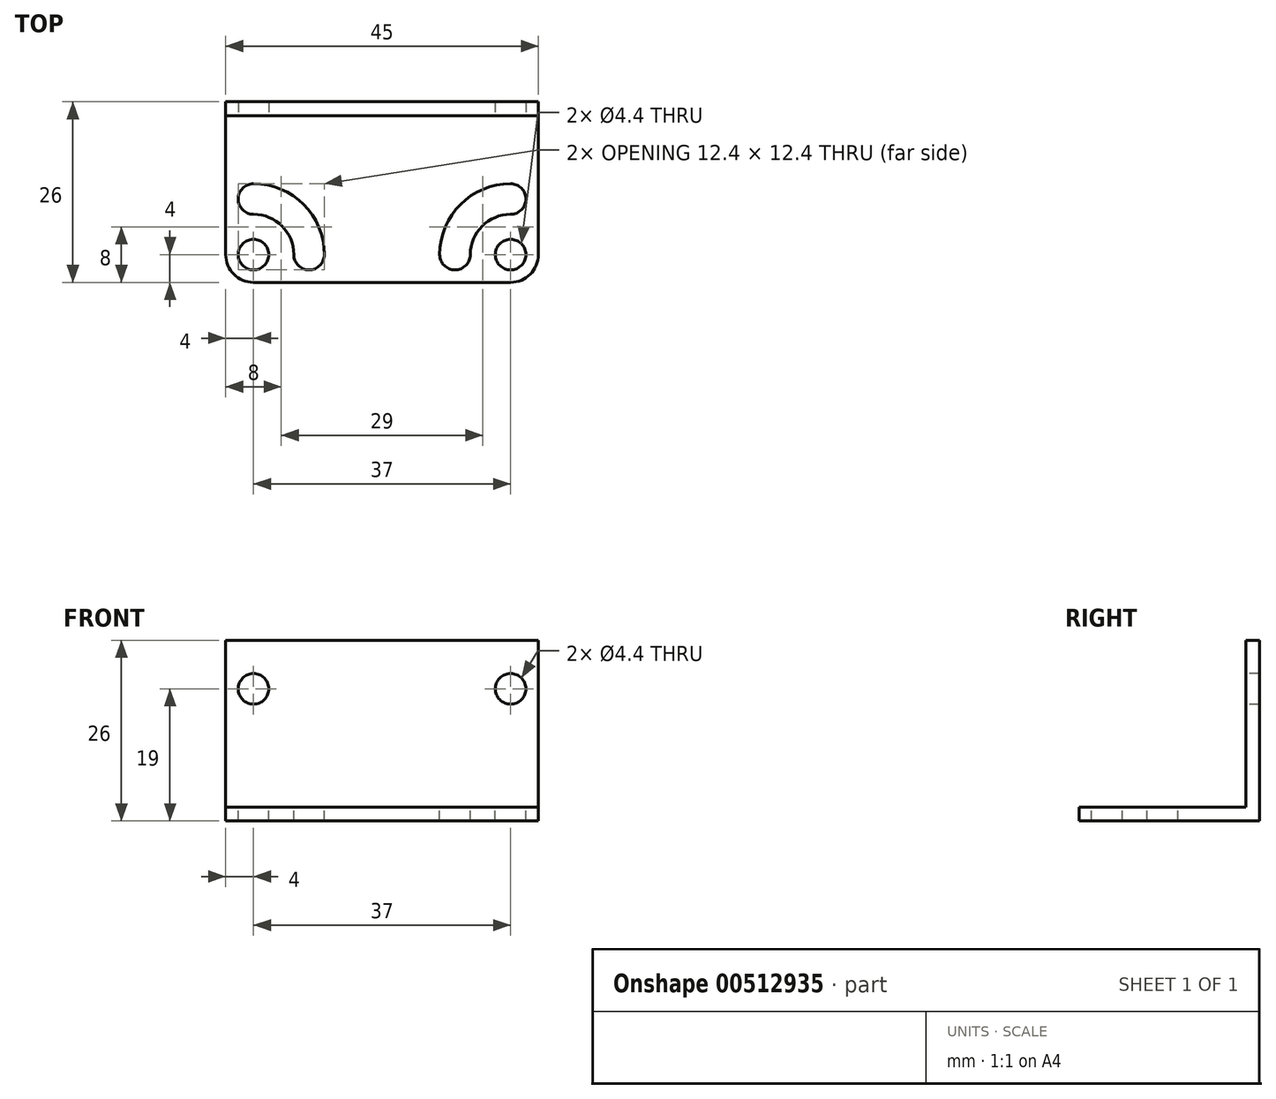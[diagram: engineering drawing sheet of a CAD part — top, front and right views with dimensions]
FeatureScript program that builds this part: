
annotation { "Feature Type Name" : "Feature", "Feature Type Description" : "" }
export const myFeature = defineFeature(function(context is Context, id is Id, definition is map)
    precondition{}
    {
        {
            var Q0;
            Q0=qCreatedBy(makeId("Top.planeOp"),FACE);
            var sketch = newSketch(context, id + "F0", { "sketchPlane" : qUnion([Q0])});
            skLineSegment(sketch, "E0.bottom", {"start": v(-22.5, 13) * mm, "end": v(22.5, 13) * mm});
            skLineSegment(sketch, "E0.top", {"start": v(-22.5, -13) * mm, "end": v(22.5, -13) * mm});
            skLineSegment(sketch, "E0.left", {"start": v(-22.5, 13) * mm, "end": v(-22.5, -13) * mm});
            skLineSegment(sketch, "E0.right", {"start": v(22.5, 13) * mm, "end": v(22.5, -13) * mm});
            skSolve(sketch);
        }
        {
            var Q0;
            Q0 = qSketchRegion(id + "F0", true);
            extrude(context, id + "F1", {"entities" : qUnion([Q0]), "depth" : 26 * mm});
        }
        {
            var Q0;
            Q0=makeQuery(id+"F1.opExtrude","SWEPT_FACE",FACE,{"disambiguationData":[OSD([sQuery(id+"F0.wireOp",EDGE,"E0.right")])]});
            var sketch = newSketch(context, id + "F2", { "sketchPlane" : qUnion([Q0])});
            skLineSegment(sketch, "E1.bottom", {"start": v(-13, 26) * mm, "end": v(11, 26) * mm});
            skLineSegment(sketch, "E1.top", {"start": v(-13, 2) * mm, "end": v(11, 2) * mm});
            skLineSegment(sketch, "E1.left", {"start": v(-13, 26) * mm, "end": v(-13, 2) * mm});
            skLineSegment(sketch, "E1.right", {"start": v(11, 26) * mm, "end": v(11, 2) * mm});
            skSolve(sketch);
        }
        {
            var Q0;
            Q0 = qSketchRegion(id + "F2", true);
            extrude(context, id + "F3", {"entities" : qUnion([Q0]), "operationType" : NewBodyOperationType.REMOVE, "endBound" : BoundingType.THROUGH_ALL, "oppositeDirection" : true, "depth" : 25 * mm});
        }
        {
            var Q0;
            Q0=makeQuery(id+"F3.boolean.opBoolean","COPY",FACE,{"derivedFrom":makeQuery(id+"F3.opExtrude","SWEPT_FACE",FACE,{"disambiguationData":[OSD([sQuery(id+"F2.wireOp",EDGE,"E1.top")])]})});
            var sketch = newSketch(context, id + "F4", { "sketchPlane" : qUnion([Q0])});
            skPoint(sketch, "E2", {"position": v(-18.5, -9) * mm});
            skPoint(sketch, "E3", {"position": v(-12.98, -3.21) * mm});
            skPoint(sketch, "E4.MirrorP", {"position": v(18.5, -9) * mm});
            skSolve(sketch);
        }
        {
            var Q0;
            Q0=sQuery(id+"F4.wireOp",VERTEX,"E2");
            var Q1;
            Q1=sQuery(id+"F4.wireOp",VERTEX,"E4.MirrorP");
            var Q2;
            Q2=makeQuery(id+"F1.opExtrude","SWEPT_BODY",BODY,{"disambiguationData":[OSD([sQuery(id+"F0.wireOp",EDGE,"E0.bottom"),sQuery(id+"F0.wireOp",EDGE,"E0.top"),sQuery(id+"F0.wireOp",EDGE,"E0.left"),sQuery(id+"F0.wireOp",EDGE,"E0.right")])]});
            hole(context, id + "F5", {"style" : HoleStyle.SIMPLE, "endStyle" : HoleEndStyle.THROUGH, "standardTappedOrClearance" : lookupTablePath({ "standard" : "ISO", "fit" : "Normal", "size" : "M4", "type" : "Clearance" }), "standardBlindInLast" : lookupTablePath({ "fit" : "Standard", "standard" : "ISO", "size" : "M4", "type" : "Clearance" }), "holeDiameter" : 4.4 * mm, "isTappedThrough" : true, "tappedDepth" : 12 * mm, "tapClearance" : 3, "locations" : qUnion([Q0, Q1]), "scope" : qUnion([Q2])});
        }
        {
            var Q0;
            Q0=makeQuery(id+"F3.boolean.opBoolean","COPY",FACE,{"derivedFrom":makeQuery(id+"F3.opExtrude","SWEPT_FACE",FACE,{"disambiguationData":[OSD([sQuery(id+"F2.wireOp",EDGE,"E1.right")])]})});
            var sketch = newSketch(context, id + "F6", { "sketchPlane" : qUnion([Q0])});
            skPoint(sketch, "E5", {"position": v(-18.5, 19) * mm});
            skPoint(sketch, "E6", {"position": v(18.5, 19) * mm});
            skSolve(sketch);
        }
        {
            var Q0;
            Q0=sQuery(id+"F6.wireOp",VERTEX,"E5");
            var Q1;
            Q1=sQuery(id+"F6.wireOp",VERTEX,"E6");
            var Q2;
            Q2=makeQuery(id+"F1.opExtrude","SWEPT_BODY",BODY,{"disambiguationData":[OSD([sQuery(id+"F0.wireOp",EDGE,"E0.bottom"),sQuery(id+"F0.wireOp",EDGE,"E0.top"),sQuery(id+"F0.wireOp",EDGE,"E0.left"),sQuery(id+"F0.wireOp",EDGE,"E0.right")])]});
            hole(context, id + "F7", {"style" : HoleStyle.SIMPLE, "endStyle" : HoleEndStyle.THROUGH, "standardTappedOrClearance" : lookupTablePath({ "standard" : "ISO", "fit" : "Normal", "size" : "M4", "type" : "Clearance" }), "standardBlindInLast" : lookupTablePath({ "fit" : "Standard", "standard" : "ISO", "size" : "M4", "type" : "Clearance" }), "holeDiameter" : 4.4 * mm, "isTappedThrough" : true, "tappedDepth" : 12 * mm, "tapClearance" : 3, "locations" : qUnion([Q0, Q1]), "scope" : qUnion([Q2])});
        }
        {
            var Q0;
            Q0=makeQuery(id+"F3.boolean.opBoolean","COPY",FACE,{"derivedFrom":makeQuery(id+"F3.opExtrude","SWEPT_FACE",FACE,{"disambiguationData":[OSD([sQuery(id+"F2.wireOp",EDGE,"E1.top")])]})});
            var sketch = newSketch(context, id + "F8", { "sketchPlane" : qUnion([Q0])});
            skArc(sketch, "E7", {"start": v(-10.5, -9) * mm, "mid": v(-12.84, -3.34) * mm, "end": v(-18.5, -1) * mm, "construction": true});
            skArc(sketch, "E8", {"start": v(-8.3, -9) * mm, "mid": v(-11.29, -1.79) * mm, "end": v(-18.5, 1.2) * mm});
            skArc(sketch, "E9", {"start": v(-12.7, -9) * mm, "mid": v(-14.4, -4.9) * mm, "end": v(-18.5, -3.2) * mm});
            skArc(sketch, "E10", {"start": v(-18.5, 1.2) * mm, "mid": v(-20.7, -1) * mm, "end": v(-18.5, -3.2) * mm});
            skArc(sketch, "E11", {"start": v(-8.3, -9) * mm, "mid": v(-10.5, -11.2) * mm, "end": v(-12.7, -9) * mm});
            skArc(sketch, "E12.MirrorCS", {"start": v(8.3, -9) * mm, "mid": v(11.29, -1.79) * mm, "end": v(18.5, 1.2) * mm});
            skArc(sketch, "E13.MirrorCS", {"start": v(8.3, -9) * mm, "mid": v(10.5, -11.2) * mm, "end": v(12.7, -9) * mm});
            skArc(sketch, "E14.MirrorCS", {"start": v(12.7, -9) * mm, "mid": v(14.4, -4.9) * mm, "end": v(18.5, -3.2) * mm});
            skArc(sketch, "E15.MirrorCS", {"start": v(18.5, 1.2) * mm, "mid": v(20.7, -1) * mm, "end": v(18.5, -3.2) * mm});
            skArc(sketch, "E16.MirrorCS", {"start": v(10.5, -9) * mm, "mid": v(12.84, -3.34) * mm, "end": v(18.5, -1) * mm, "construction": true});
            skSolve(sketch);
        }
        {
            var Q0;
            Q0 = qSketchRegion(id + "F8", true);
            extrude(context, id + "F9", {"entities" : qUnion([Q0]), "operationType" : NewBodyOperationType.REMOVE, "endBound" : BoundingType.THROUGH_ALL, "oppositeDirection" : true, "depth" : 25 * mm});
        }
        {
            var Q0;
            Q0=makeQuery(id+"F1.opExtrude","SWEPT_EDGE",EDGE,{"disambiguationData":[OSD([sQuery(id+"F0.wireOp",EDGE,"E0.top"),sQuery(id+"F0.wireOp",EDGE,"E0.left")])]});
            var Q1;
            Q1=makeQuery(id+"F1.opExtrude","SWEPT_EDGE",EDGE,{"disambiguationData":[OSD([sQuery(id+"F0.wireOp",EDGE,"E0.top"),sQuery(id+"F0.wireOp",EDGE,"E0.right")])]});
            fillet(context, id + "F10", {"entities" : qUnion([Q0, Q1]), "radius" : 4 * mm, "tangentPropagation" : true, "allowEdgeOverflow" : false});
        }
    });
